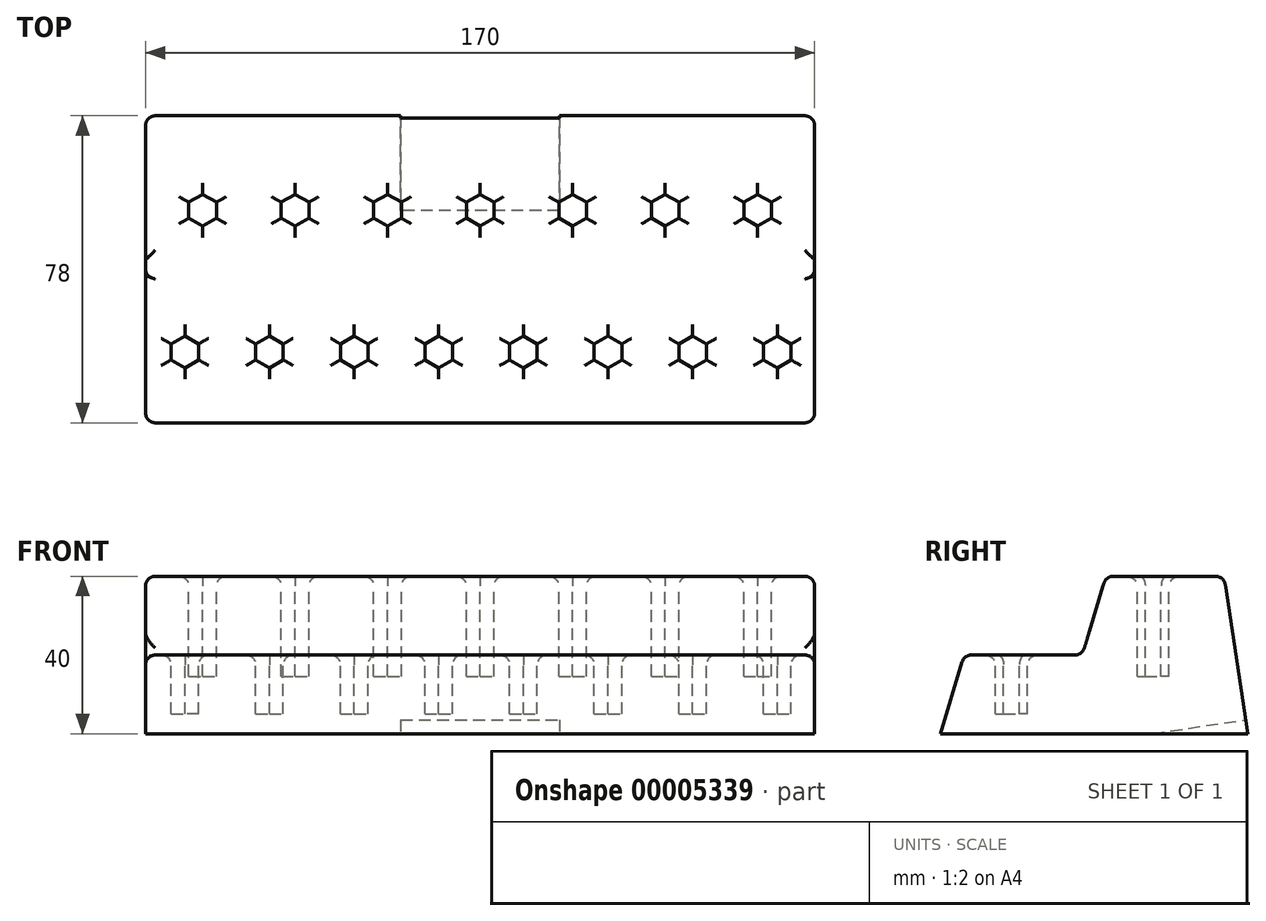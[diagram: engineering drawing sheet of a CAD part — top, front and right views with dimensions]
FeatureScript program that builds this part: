
annotation { "Feature Type Name" : "Feature", "Feature Type Description" : "" }
export const myFeature = defineFeature(function(context is Context, id is Id, definition is map)
    precondition{}
    {
        {
            var Q0;
            Q0=qCreatedBy(makeId("Right.planeOp"),FACE);
            var sketch = newSketch(context, id + "F0", { "sketchPlane" : qUnion([Q0])});
            skLineSegment(sketch, "E0", {"start": v(0, 0) * mm, "end": v(6, 20) * mm});
            skLineSegment(sketch, "E1", {"start": v(6, 20) * mm, "end": v(36, 20) * mm});
            skLineSegment(sketch, "E2", {"start": v(36, 20) * mm, "end": v(42, 40) * mm});
            skLineSegment(sketch, "E3", {"start": v(42, 40) * mm, "end": v(72, 40) * mm});
            skLineSegment(sketch, "E4", {"start": v(72, 40) * mm, "end": v(78, 0) * mm});
            skLineSegment(sketch, "E5", {"start": v(78, 0) * mm, "end": v(0, 0) * mm});
            skLineSegment(sketch, "E6", {"start": v(6, 20) * mm, "end": v(6, 0) * mm});
            skLineSegment(sketch, "E7", {"start": v(72, 40) * mm, "end": v(72, 0) * mm});
            skSolve(sketch);
        }
        {
            var Q0;
            {var subQ2=sQuery(id+"F0.wireOp",EDGE,"E0");Q0=makeQuery(id+"F0.imprint","IMPRINT",FACE,{"disambiguationData":[TD([[makeQuery(id+"F0.imprint","IMPRINT",EDGE,{"derivedFrom":subQ2}),-1.0]])]});}
            var Q1;
            {var subQ2=sQuery(id+"F0.wireOp",EDGE,"E4");Q1=makeQuery(id+"F0.imprint","IMPRINT",FACE,{"disambiguationData":[TD([[makeQuery(id+"F0.imprint","IMPRINT",EDGE,{"derivedFrom":subQ2}),-1.0]])]});}
            var Q2;
            Q2=makeQuery(id+"F0.imprint","IMPRINT",FACE,{"disambiguationData":[TD([[makeQuery(id+"F0.imprint","IMPRINT",EDGE,{"derivedFrom":sQuery(id+"F0.wireOp",EDGE,"E1")}),-1.0]])]});
            extrude(context, id + "F1", {"entities" : qUnion([Q0, Q1, Q2]), "endBound" : BoundingType.SYMMETRIC, "depth" : 170 * mm});
        }
        {
            var Q0;
            Q0=makeQuery(id+"F1.opExtrude","SWEPT_FACE",FACE,{"disambiguationData":[OSD([sQuery(id+"F0.wireOp",EDGE,"E3")])]});
            var sketch = newSketch(context, id + "F2", { "sketchPlane" : qUnion([Q0])});
            skCircle(sketch, "E8.cCircle", {"center": v(-70.5, 54) * mm, "radius": 3.5 * mm, "construction": true});
            skLineSegment(sketch, "E8.0", {"start": v(-67, 56.02) * mm, "end": v(-67, 51.98) * mm});
            skLineSegment(sketch, "E8.1", {"start": v(-67, 51.98) * mm, "end": v(-70.5, 49.96) * mm});
            skLineSegment(sketch, "E8.2", {"start": v(-70.5, 49.96) * mm, "end": v(-74, 51.98) * mm});
            skLineSegment(sketch, "E8.3", {"start": v(-74, 51.98) * mm, "end": v(-74, 56.02) * mm});
            skLineSegment(sketch, "E8.4", {"start": v(-74, 56.02) * mm, "end": v(-70.5, 58.04) * mm});
            skLineSegment(sketch, "E8.5", {"start": v(-70.5, 58.04) * mm, "end": v(-67, 56.02) * mm});
            skPoint(sketch, "E8.0.midPoint", {"position": v(-67, 54) * mm});
            skLineSegment(sketch, "E9.1.0.0", {"start": v(-47, 58.04) * mm, "end": v(-43.5, 56.02) * mm});
            skLineSegment(sketch, "E9.1.0.1", {"start": v(-50.5, 56.02) * mm, "end": v(-47, 58.04) * mm});
            skLineSegment(sketch, "E9.1.0.2", {"start": v(-50.5, 51.98) * mm, "end": v(-50.5, 56.02) * mm});
            skLineSegment(sketch, "E9.1.0.3", {"start": v(-47, 49.96) * mm, "end": v(-50.5, 51.98) * mm});
            skLineSegment(sketch, "E9.1.0.4", {"start": v(-43.5, 51.98) * mm, "end": v(-47, 49.96) * mm});
            skLineSegment(sketch, "E9.1.0.5", {"start": v(-43.5, 56.02) * mm, "end": v(-43.5, 51.98) * mm});
            skPoint(sketch, "E9.1.0.6", {"position": v(-43.5, 54) * mm});
            skLineSegment(sketch, "E9.2.0.0", {"start": v(-23.5, 58.04) * mm, "end": v(-20, 56.02) * mm});
            skLineSegment(sketch, "E9.2.0.1", {"start": v(-27, 56.02) * mm, "end": v(-23.5, 58.04) * mm});
            skLineSegment(sketch, "E9.2.0.2", {"start": v(-27, 51.98) * mm, "end": v(-27, 56.02) * mm});
            skLineSegment(sketch, "E9.2.0.3", {"start": v(-23.5, 49.96) * mm, "end": v(-27, 51.98) * mm});
            skLineSegment(sketch, "E9.2.0.4", {"start": v(-20, 51.98) * mm, "end": v(-23.5, 49.96) * mm});
            skLineSegment(sketch, "E9.2.0.5", {"start": v(-20, 56.02) * mm, "end": v(-20, 51.98) * mm});
            skPoint(sketch, "E9.2.0.6", {"position": v(-20, 54) * mm});
            skLineSegment(sketch, "E9.3.0.0", {"start": v(0, 58.04) * mm, "end": v(3.5, 56.02) * mm});
            skLineSegment(sketch, "E9.3.0.1", {"start": v(-3.5, 56.02) * mm, "end": v(0, 58.04) * mm});
            skLineSegment(sketch, "E9.3.0.2", {"start": v(-3.5, 51.98) * mm, "end": v(-3.5, 56.02) * mm});
            skLineSegment(sketch, "E9.3.0.3", {"start": v(0, 49.96) * mm, "end": v(-3.5, 51.98) * mm});
            skLineSegment(sketch, "E9.3.0.4", {"start": v(3.5, 51.98) * mm, "end": v(0, 49.96) * mm});
            skLineSegment(sketch, "E9.3.0.5", {"start": v(3.5, 56.02) * mm, "end": v(3.5, 51.98) * mm});
            skPoint(sketch, "E9.3.0.6", {"position": v(3.5, 54) * mm});
            skLineSegment(sketch, "E9.4.0.0", {"start": v(23.5, 58.04) * mm, "end": v(27, 56.02) * mm});
            skLineSegment(sketch, "E9.4.0.1", {"start": v(20, 56.02) * mm, "end": v(23.5, 58.04) * mm});
            skLineSegment(sketch, "E9.4.0.2", {"start": v(20, 51.98) * mm, "end": v(20, 56.02) * mm});
            skLineSegment(sketch, "E9.4.0.3", {"start": v(23.5, 49.96) * mm, "end": v(20, 51.98) * mm});
            skLineSegment(sketch, "E9.4.0.4", {"start": v(27, 51.98) * mm, "end": v(23.5, 49.96) * mm});
            skLineSegment(sketch, "E9.4.0.5", {"start": v(27, 56.02) * mm, "end": v(27, 51.98) * mm});
            skPoint(sketch, "E9.4.0.6", {"position": v(27, 54) * mm});
            skLineSegment(sketch, "E9.5.0.0", {"start": v(47, 58.04) * mm, "end": v(50.5, 56.02) * mm});
            skLineSegment(sketch, "E9.5.0.1", {"start": v(43.5, 56.02) * mm, "end": v(47, 58.04) * mm});
            skLineSegment(sketch, "E9.5.0.2", {"start": v(43.5, 51.98) * mm, "end": v(43.5, 56.02) * mm});
            skLineSegment(sketch, "E9.5.0.3", {"start": v(47, 49.96) * mm, "end": v(43.5, 51.98) * mm});
            skLineSegment(sketch, "E9.5.0.4", {"start": v(50.5, 51.98) * mm, "end": v(47, 49.96) * mm});
            skLineSegment(sketch, "E9.5.0.5", {"start": v(50.5, 56.02) * mm, "end": v(50.5, 51.98) * mm});
            skPoint(sketch, "E9.5.0.6", {"position": v(50.5, 54) * mm});
            skLineSegment(sketch, "E9.6.0.0", {"start": v(70.5, 58.04) * mm, "end": v(74, 56.02) * mm});
            skLineSegment(sketch, "E9.6.0.1", {"start": v(67, 56.02) * mm, "end": v(70.5, 58.04) * mm});
            skLineSegment(sketch, "E9.6.0.2", {"start": v(67, 51.98) * mm, "end": v(67, 56.02) * mm});
            skLineSegment(sketch, "E9.6.0.3", {"start": v(70.5, 49.96) * mm, "end": v(67, 51.98) * mm});
            skLineSegment(sketch, "E9.6.0.4", {"start": v(74, 51.98) * mm, "end": v(70.5, 49.96) * mm});
            skLineSegment(sketch, "E9.6.0.5", {"start": v(74, 56.02) * mm, "end": v(74, 51.98) * mm});
            skPoint(sketch, "E9.6.0.6", {"position": v(74, 54) * mm});
            skLineSegment(sketch, "E9.direction1", {"start": v(-70.5, 58.04) * mm, "end": v(-47, 58.04) * mm, "construction": true});
            skSolve(sketch);
        }
        {
            var Q0;
            Q0 = qSketchRegion(id + "F2", true);
            extrude(context, id + "F3", {"entities" : qUnion([Q0]), "operationType" : NewBodyOperationType.REMOVE, "oppositeDirection" : true, "depth" : 25.4 * mm});
        }
        {
            var Q0;
            Q0=makeQuery(id+"F1.opExtrude","SWEPT_FACE",FACE,{"disambiguationData":[OSD([sQuery(id+"F0.wireOp",EDGE,"E1")])]});
            var sketch = newSketch(context, id + "F4", { "sketchPlane" : qUnion([Q0])});
            skCircle(sketch, "E10.cCircle", {"center": v(-75, 18) * mm, "radius": 3.5 * mm, "construction": true});
            skLineSegment(sketch, "E10.0", {"start": v(-71.5, 15.98) * mm, "end": v(-75, 13.96) * mm});
            skLineSegment(sketch, "E10.1", {"start": v(-75, 13.96) * mm, "end": v(-78.5, 15.98) * mm});
            skLineSegment(sketch, "E10.2", {"start": v(-78.5, 15.98) * mm, "end": v(-78.5, 20.02) * mm});
            skLineSegment(sketch, "E10.3", {"start": v(-78.5, 20.02) * mm, "end": v(-75, 22.04) * mm});
            skLineSegment(sketch, "E10.4", {"start": v(-75, 22.04) * mm, "end": v(-71.5, 20.02) * mm});
            skLineSegment(sketch, "E10.5", {"start": v(-71.5, 20.02) * mm, "end": v(-71.5, 15.98) * mm});
            skPoint(sketch, "E10.0.midPoint", {"position": v(-73.25, 14.97) * mm});
            skLineSegment(sketch, "E11.1.0.0", {"start": v(-53.5, 22.04) * mm, "end": v(-50, 20.02) * mm});
            skLineSegment(sketch, "E11.1.0.1", {"start": v(-57, 20.02) * mm, "end": v(-53.5, 22.04) * mm});
            skLineSegment(sketch, "E11.1.0.2", {"start": v(-57, 15.98) * mm, "end": v(-57, 20.02) * mm});
            skLineSegment(sketch, "E11.1.0.3", {"start": v(-53.5, 13.96) * mm, "end": v(-57, 15.98) * mm});
            skLineSegment(sketch, "E11.1.0.4", {"start": v(-50, 15.98) * mm, "end": v(-53.5, 13.96) * mm});
            skLineSegment(sketch, "E11.1.0.5", {"start": v(-50, 20.02) * mm, "end": v(-50, 15.98) * mm});
            skLineSegment(sketch, "E11.2.0.0", {"start": v(-32, 22.04) * mm, "end": v(-28.5, 20.02) * mm});
            skLineSegment(sketch, "E11.2.0.1", {"start": v(-35.5, 20.02) * mm, "end": v(-32, 22.04) * mm});
            skLineSegment(sketch, "E11.2.0.2", {"start": v(-35.5, 15.98) * mm, "end": v(-35.5, 20.02) * mm});
            skLineSegment(sketch, "E11.2.0.3", {"start": v(-32, 13.96) * mm, "end": v(-35.5, 15.98) * mm});
            skLineSegment(sketch, "E11.2.0.4", {"start": v(-28.5, 15.98) * mm, "end": v(-32, 13.96) * mm});
            skLineSegment(sketch, "E11.2.0.5", {"start": v(-28.5, 20.02) * mm, "end": v(-28.5, 15.98) * mm});
            skLineSegment(sketch, "E11.3.0.0", {"start": v(-10.5, 22.04) * mm, "end": v(-7, 20.02) * mm});
            skLineSegment(sketch, "E11.3.0.1", {"start": v(-14, 20.02) * mm, "end": v(-10.5, 22.04) * mm});
            skLineSegment(sketch, "E11.3.0.2", {"start": v(-14, 15.98) * mm, "end": v(-14, 20.02) * mm});
            skLineSegment(sketch, "E11.3.0.3", {"start": v(-10.5, 13.96) * mm, "end": v(-14, 15.98) * mm});
            skLineSegment(sketch, "E11.3.0.4", {"start": v(-7, 15.98) * mm, "end": v(-10.5, 13.96) * mm});
            skLineSegment(sketch, "E11.3.0.5", {"start": v(-7, 20.02) * mm, "end": v(-7, 15.98) * mm});
            skLineSegment(sketch, "E11.4.0.0", {"start": v(11, 22.04) * mm, "end": v(14.5, 20.02) * mm});
            skLineSegment(sketch, "E11.4.0.1", {"start": v(7.5, 20.02) * mm, "end": v(11, 22.04) * mm});
            skLineSegment(sketch, "E11.4.0.2", {"start": v(7.5, 15.98) * mm, "end": v(7.5, 20.02) * mm});
            skLineSegment(sketch, "E11.4.0.3", {"start": v(11, 13.96) * mm, "end": v(7.5, 15.98) * mm});
            skLineSegment(sketch, "E11.4.0.4", {"start": v(14.5, 15.98) * mm, "end": v(11, 13.96) * mm});
            skLineSegment(sketch, "E11.4.0.5", {"start": v(14.5, 20.02) * mm, "end": v(14.5, 15.98) * mm});
            skLineSegment(sketch, "E11.5.0.0", {"start": v(32.5, 22.04) * mm, "end": v(36, 20.02) * mm});
            skLineSegment(sketch, "E11.5.0.1", {"start": v(29, 20.02) * mm, "end": v(32.5, 22.04) * mm});
            skLineSegment(sketch, "E11.5.0.2", {"start": v(29, 15.98) * mm, "end": v(29, 20.02) * mm});
            skLineSegment(sketch, "E11.5.0.3", {"start": v(32.5, 13.96) * mm, "end": v(29, 15.98) * mm});
            skLineSegment(sketch, "E11.5.0.4", {"start": v(36, 15.98) * mm, "end": v(32.5, 13.96) * mm});
            skLineSegment(sketch, "E11.5.0.5", {"start": v(36, 20.02) * mm, "end": v(36, 15.98) * mm});
            skLineSegment(sketch, "E11.6.0.0", {"start": v(54, 22.04) * mm, "end": v(57.5, 20.02) * mm});
            skLineSegment(sketch, "E11.6.0.1", {"start": v(50.5, 20.02) * mm, "end": v(54, 22.04) * mm});
            skLineSegment(sketch, "E11.6.0.2", {"start": v(50.5, 15.98) * mm, "end": v(50.5, 20.02) * mm});
            skLineSegment(sketch, "E11.6.0.3", {"start": v(54, 13.96) * mm, "end": v(50.5, 15.98) * mm});
            skLineSegment(sketch, "E11.6.0.4", {"start": v(57.5, 15.98) * mm, "end": v(54, 13.96) * mm});
            skLineSegment(sketch, "E11.6.0.5", {"start": v(57.5, 20.02) * mm, "end": v(57.5, 15.98) * mm});
            skLineSegment(sketch, "E11.7.0.0", {"start": v(75.5, 22.04) * mm, "end": v(79, 20.02) * mm});
            skLineSegment(sketch, "E11.7.0.1", {"start": v(72, 20.02) * mm, "end": v(75.5, 22.04) * mm});
            skLineSegment(sketch, "E11.7.0.2", {"start": v(72, 15.98) * mm, "end": v(72, 20.02) * mm});
            skLineSegment(sketch, "E11.7.0.3", {"start": v(75.5, 13.96) * mm, "end": v(72, 15.98) * mm});
            skLineSegment(sketch, "E11.7.0.4", {"start": v(79, 15.98) * mm, "end": v(75.5, 13.96) * mm});
            skLineSegment(sketch, "E11.7.0.5", {"start": v(79, 20.02) * mm, "end": v(79, 15.98) * mm});
            skLineSegment(sketch, "E11.direction1", {"start": v(-53.5, 22.04) * mm, "end": v(-32, 22.04) * mm, "construction": true});
            skSolve(sketch);
        }
        {
            var Q0;
            Q0 = qSketchRegion(id + "F4", true);
            extrude(context, id + "F5", {"entities" : qUnion([Q0]), "operationType" : NewBodyOperationType.REMOVE, "oppositeDirection" : true, "depth" : 15 * mm});
        }
        {
            var Q0;
            Q0=makeQuery(id+"F1.opExtrude","SWEPT_FACE",FACE,{"disambiguationData":[OSD([sQuery(id+"F0.wireOp",EDGE,"E1")])]});
            var Q1;
            Q1=makeQuery(id+"F1.opExtrude","SWEPT_FACE",FACE,{"disambiguationData":[OSD([sQuery(id+"F0.wireOp",EDGE,"E3")])]});
            var Q2;
            Q2=makeQuery(id+"F1.opExtrude","CAP_EDGE",EDGE,{"disambiguationData":[OSD([sQuery(id+"F0.wireOp",EDGE,"E0")])],"isStart":true});
            var Q3;
            Q3=makeQuery(id+"F1.opExtrude","CAP_EDGE",EDGE,{"disambiguationData":[OSD([sQuery(id+"F0.wireOp",EDGE,"E0")])],"isStart":false});
            var Q4;
            Q4=makeQuery(id+"F1.opExtrude","CAP_EDGE",EDGE,{"disambiguationData":[OSD([sQuery(id+"F0.wireOp",EDGE,"E4")])],"isStart":true});
            var Q5;
            Q5=makeQuery(id+"F1.opExtrude","CAP_EDGE",EDGE,{"disambiguationData":[OSD([sQuery(id+"F0.wireOp",EDGE,"E4")])],"isStart":false});
            fillet(context, id + "F6", {"entities" : qUnion([Q0, Q1, Q2, Q3, Q4, Q5]), "radius" : 2.5 * mm, "tangentPropagation" : true, "allowEdgeOverflow" : false});
        }
        {
            var Q0;
            Q0=makeQuery(id+"F1.opExtrude","SWEPT_BODY",BODY,{"disambiguationData":[OSD([sQuery(id+"F0.wireOp",EDGE,"E0"),sQuery(id+"F0.wireOp",EDGE,"E1"),sQuery(id+"F0.wireOp",EDGE,"E2"),sQuery(id+"F0.wireOp",EDGE,"E3"),sQuery(id+"F0.wireOp",EDGE,"E4"),sQuery(id+"F0.wireOp",EDGE,"E5")])]});
            transform(context, id + "F7", {"entities" : qUnion([Q0]), "transformType" : TransformType.TRANSLATION_3D, "dx" : 0 * mm, "dy" : 100 * mm, "dz" : 0 * mm, "makeCopy" : true});
        }
        {
            var Q0;
            Q0=makeQuery(id+"F7.opPattern","COPY",BODY,{"derivedFrom":makeQuery(id+"F1.opExtrude","SWEPT_BODY",BODY,{"disambiguationData":[OSD([sQuery(id+"F0.wireOp",EDGE,"E0"),sQuery(id+"F0.wireOp",EDGE,"E1"),sQuery(id+"F0.wireOp",EDGE,"E2"),sQuery(id+"F0.wireOp",EDGE,"E3"),sQuery(id+"F0.wireOp",EDGE,"E4"),sQuery(id+"F0.wireOp",EDGE,"E5")])]}),"instanceName":"1"});
            deleteBodies(context, id + "F8", {"entities" : qUnion([Q0])});
        }
        {
            var Q0;
            Q0=makeQuery(id+"F1.opExtrude","SWEPT_FACE",FACE,{"disambiguationData":[OSD([sQuery(id+"F0.wireOp",EDGE,"E4")])]});
            var sketch = newSketch(context, id + "F9", { "sketchPlane" : qUnion([Q0])});
            skLineSegment(sketch, "E12.rect.bottom", {"start": v(20.15, -8) * mm, "end": v(-20.15, -8) * mm});
            skLineSegment(sketch, "E12.rect.top", {"start": v(20.15, -15.15) * mm, "end": v(-20.15, -15.15) * mm});
            skLineSegment(sketch, "E12.rect.left", {"start": v(20.15, -8) * mm, "end": v(20.15, -15.15) * mm});
            skLineSegment(sketch, "E12.rect.right", {"start": v(-20.15, -8) * mm, "end": v(-20.15, -15.15) * mm});
            skPoint(sketch, "E12.rect.middle", {"position": v(0, -11.57) * mm});
            skSolve(sketch);
        }
        {
            var Q0;
            {var subQ5=sQuery(id+"F9.wireOp",EDGE,"E12.rect.bottom");Q0=makeQuery(id+"F9.imprint","IMPRINT",FACE,{"disambiguationData":[TD([[makeQuery(id+"F9.imprint","IMPRINT",EDGE,{"derivedFrom":subQ5}),1.0]])]});}
            extrude(context, id + "F10", {"entities" : qUnion([Q0]), "operationType" : NewBodyOperationType.REMOVE, "endBound" : BoundingType.THROUGH_ALL, "oppositeDirection" : true, "depth" : 25 * mm});
        }
    });
